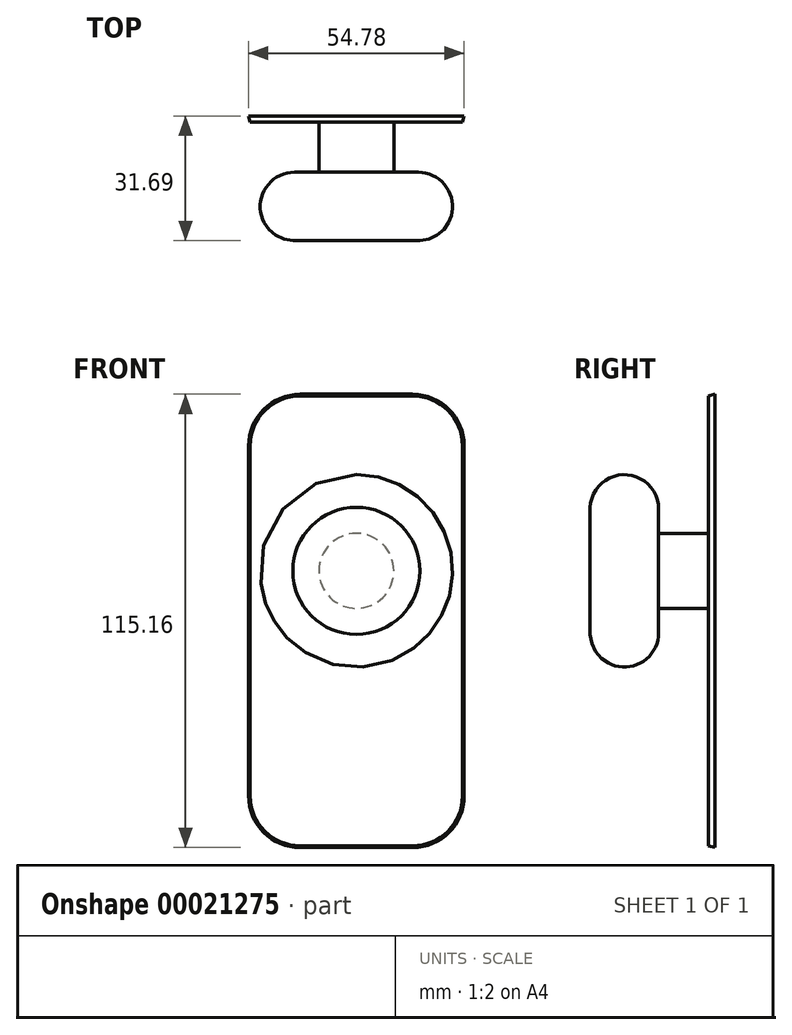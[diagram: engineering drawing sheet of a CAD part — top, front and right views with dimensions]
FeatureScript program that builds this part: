
annotation { "Feature Type Name" : "Feature", "Feature Type Description" : "" }
export const myFeature = defineFeature(function(context is Context, id is Id, definition is map)
    precondition{}
    {
        {
            var Q0;
            Q0=qCreatedBy(makeId("Top.planeOp"),FACE);
            var sketch = newSketch(context, id + "F0", { "sketchPlane" : qUnion([Q0])});
            skLineSegment(sketch, "E0", {"start": v(9.53, 0) * mm, "end": v(9.53, -12.7) * mm});
            skLineSegment(sketch, "E1", {"start": v(0, -30.1) * mm, "end": v(16.15, -30.1) * mm});
            skLineSegment(sketch, "E2", {"start": v(9.53, -12.7) * mm, "end": v(15.75, -12.7) * mm});
            skArc(sketch, "E3", {"start": v(16.15, -30.1) * mm, "mid": v(24.45, -21.2) * mm, "end": v(15.75, -12.7) * mm});
            skLineSegment(sketch, "E4", {"start": v(9.53, 0) * mm, "end": v(0, 0) * mm});
            skLineSegment(sketch, "E5", {"start": v(0, 0) * mm, "end": v(0, -30.1) * mm});
            skSolve(sketch);
        }
        {
            var Q0;
            Q0=qCreatedBy(makeId("Top.planeOp"),FACE);
            var sketch = newSketch(context, id + "F1", { "sketchPlane" : qUnion([Q0])});
            skLineSegment(sketch, "E6", {"start": v(0, 60.47) * mm, "end": v(0, -71.02) * mm});
            skSolve(sketch);
        }
        {
            var Q0;
            Q0 = qSketchRegion(id + "F0", true);
            var Q1;
            Q1=sQuery(id+"F1.wireOp",EDGE,"E6");
            revolve(context, id + "F2", {"entities" : qUnion([Q0]), "axis" : qUnion([Q1]), "revolveType" : RevolveType.FULL});
        }
        {
            var Q0;
            Q0=makeQuery(id+"F2.opRevolve","SWEPT_FACE",FACE,{"disambiguationData":[OSD([sQuery(id+"F0.wireOp",EDGE,"E4")])]});
            var sketch = newSketch(context, id + "F3", { "sketchPlane" : qUnion([Q0])});
            skLineSegment(sketch, "E7.rect.bottom", {"start": v(14.26, 44.45) * mm, "end": v(-14.26, 44.45) * mm});
            skLineSegment(sketch, "E7.rect.top", {"start": v(14.26, -69.85) * mm, "end": v(-14.26, -69.85) * mm});
            skLineSegment(sketch, "E7.rect.left", {"start": v(26.96, 31.75) * mm, "end": v(26.96, -57.15) * mm});
            skLineSegment(sketch, "E7.rect.right", {"start": v(-26.96, 31.75) * mm, "end": v(-26.96, -57.15) * mm});
            skPoint(sketch, "E7.rect.middle", {"position": v(0, -12.7) * mm});
            skPoint(sketch, "E8.visualSharp", {"position": v(-26.96, 44.45) * mm});
            skArc(sketch, "E8.filletArc", {"start": v(-14.26, 44.45) * mm, "mid": v(-23.24, 40.73) * mm, "end": v(-26.96, 31.75) * mm});
            skPoint(sketch, "E9.visualSharp", {"position": v(26.96, 44.45) * mm});
            skArc(sketch, "E9.filletArc", {"start": v(26.96, 31.75) * mm, "mid": v(23.24, 40.73) * mm, "end": v(14.26, 44.45) * mm});
            skPoint(sketch, "E10.visualSharp", {"position": v(-26.96, -69.85) * mm});
            skArc(sketch, "E10.filletArc", {"start": v(-26.96, -57.15) * mm, "mid": v(-23.24, -66.13) * mm, "end": v(-14.26, -69.85) * mm});
            skPoint(sketch, "E11.visualSharp", {"position": v(26.96, -69.85) * mm});
            skArc(sketch, "E11.filletArc", {"start": v(14.26, -69.85) * mm, "mid": v(23.24, -66.13) * mm, "end": v(26.96, -57.15) * mm});
            skSolve(sketch);
        }
        {
            var Q0;
            Q0 = qSketchRegion(id + "F3", true);
            extrude(context, id + "F4", {"entities" : qUnion([Q0]), "depth" : 1.6 * mm, "hasDraft" : true, "draftAngle" : 15 * degree});
        }
    });
